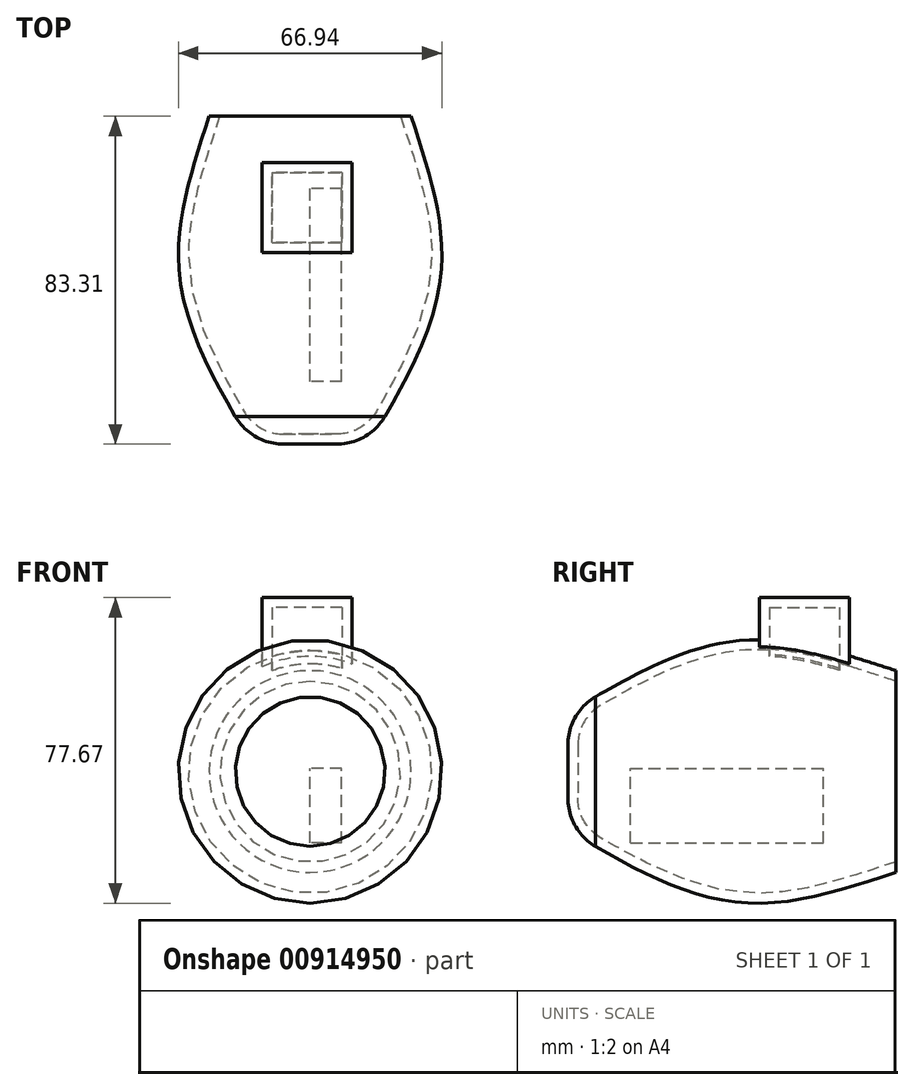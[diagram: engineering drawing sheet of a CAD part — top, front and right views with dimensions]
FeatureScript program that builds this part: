
annotation { "Feature Type Name" : "Feature", "Feature Type Description" : "" }
export const myFeature = defineFeature(function(context is Context, id is Id, definition is map)
    precondition{}
    {
        {
            var Q0;
            Q0=qCreatedBy(makeId("Front.planeOp"),FACE);
            var sketch = newSketch(context, id + "F0", { "sketchPlane" : qUnion([Q0])});
            skCircle(sketch, "E0", {"center": v(0, 0) * mm, "radius": 25.64 * mm});
            skSolve(sketch);
        }
        {
            var Q0;
            Q0=qCreatedBy(makeId("Front.planeOp"),FACE);
            cPlane(context, id + "F1", {"entities" : qUnion([Q0]), "cplaneType" : CPlaneType.OFFSET, "offset" : 38.35 * mm, "width" : 152.4 * mm, "height" : 152.4 * mm});
        }
        {
            var Q0;
            Q0=qCreatedBy(id+"F1.planeOp",FACE);
            cPlane(context, id + "F2", {"entities" : qUnion([Q0]), "cplaneType" : CPlaneType.OFFSET, "offset" : 44.96 * mm, "width" : 152.4 * mm, "height" : 152.4 * mm});
        }
        {
            var Q0;
            Q0=qCreatedBy(id+"F1.planeOp",FACE);
            var sketch = newSketch(context, id + "F3", { "sketchPlane" : qUnion([Q0])});
            skCircle(sketch, "E1", {"center": v(0, 0) * mm, "radius": 33.38 * mm});
            skSolve(sketch);
        }
        {
            var Q0;
            Q0=qCreatedBy(id+"F2.planeOp",FACE);
            var sketch = newSketch(context, id + "F4", { "sketchPlane" : qUnion([Q0])});
            skCircle(sketch, "E2", {"center": v(0, 0) * mm, "radius": 14.84 * mm});
            skSolve(sketch);
        }
        {
            var Q0;
            Q0=makeQuery(id+"F0.imprint","IMPRINT",FACE,{"disambiguationData":[TD([[makeQuery(id+"F0.imprint","IMPRINT",EDGE,{"derivedFrom":sQuery(id+"F0.wireOp",EDGE,"E0")}),1.0]])]});
            var Q1;
            Q1=makeQuery(id+"F3.imprint","IMPRINT",FACE,{"disambiguationData":[TD([[makeQuery(id+"F3.imprint","IMPRINT",EDGE,{"derivedFrom":sQuery(id+"F3.wireOp",EDGE,"E1")}),1.0]])]});
            var Q2;
            Q2=makeQuery(id+"F4.imprint","IMPRINT",FACE,{"disambiguationData":[TD([[makeQuery(id+"F4.imprint","IMPRINT",EDGE,{"derivedFrom":sQuery(id+"F4.wireOp",EDGE,"E2")}),1.0]])]});
            loft(context, id + "F5", {"sheetProfilesArray" : [{ "sheetProfileEntities" : qUnion([Q0]) }, { "sheetProfileEntities" : qUnion([Q1]) }, { "sheetProfileEntities" : qUnion([Q2]) }]});
        }
        {
            var Q0;
            Q0=makeQuery(id+"F5.opLoft","CAP_FACE",FACE,{"disambiguationData":[OSD([makeQuery(id+"F4.imprint","IMPRINT",FACE,{"disambiguationData":[TD([[makeQuery(id+"F4.imprint","IMPRINT",EDGE,{"derivedFrom":sQuery(id+"F4.wireOp",EDGE,"E2")}),1.0]])]})])],"isStart":true});
            fillet(context, id + "F6", {"entities" : qUnion([Q0]), "radius" : 14.2 * mm, "tangentPropagation" : true, "allowEdgeOverflow" : false});
        }
        {
            var Q0;
            Q0=qCreatedBy(makeId("Top.planeOp"),FACE);
            cPlane(context, id + "F7", {"entities" : qUnion([Q0]), "cplaneType" : CPlaneType.OFFSET, "offset" : 18.8 * mm, "width" : 152.4 * mm, "height" : 152.4 * mm});
        }
        {
            var Q0;
            Q0=qCreatedBy(id+"F7.planeOp",FACE);
            var sketch = newSketch(context, id + "F8", { "sketchPlane" : qUnion([Q0])});
            skLineSegment(sketch, "E3.bottom", {"start": v(10.66, -34.64) * mm, "end": v(-12.2, -34.64) * mm});
            skLineSegment(sketch, "E3.top", {"start": v(10.66, -11.78) * mm, "end": v(-12.2, -11.78) * mm});
            skLineSegment(sketch, "E3.left", {"start": v(10.66, -34.64) * mm, "end": v(10.66, -11.78) * mm});
            skLineSegment(sketch, "E3.right", {"start": v(-12.2, -34.64) * mm, "end": v(-12.2, -11.78) * mm});
            skSolve(sketch);
        }
        {
            var Q0;
            Q0 = qSketchRegion(id + "F8", true);
            extrude(context, id + "F9", {"entities" : qUnion([Q0]), "operationType" : NewBodyOperationType.ADD, "depth" : 25.4 * mm, "offsetDistance" : 25.4 * mm});
        }
        {
            var Q0;
            Q0=makeQuery(id+"F5.opLoft","CAP_FACE",FACE,{"disambiguationData":[OSD([makeQuery(id+"F0.imprint","IMPRINT",FACE,{"disambiguationData":[TD([[makeQuery(id+"F0.imprint","IMPRINT",EDGE,{"derivedFrom":sQuery(id+"F0.wireOp",EDGE,"E0")}),1.0]])]})])],"isStart":true});
            shell(context, id + "F10", {"entities" : qUnion([Q0]), "thickness" : 2.54 * mm});
        }
        {
            var Q0;
            Q0=qCreatedBy(makeId("Right.planeOp"),FACE);
            var sketch = newSketch(context, id + "F11", { "sketchPlane" : qUnion([Q0])});
            skLineSegment(sketch, "E4.bottom", {"start": v(-67.41, -18.18) * mm, "end": v(-18.41, -18.18) * mm});
            skLineSegment(sketch, "E4.top", {"start": v(-67.41, 0.82) * mm, "end": v(-18.41, 0.82) * mm});
            skLineSegment(sketch, "E4.left", {"start": v(-67.41, -18.18) * mm, "end": v(-67.41, 0.82) * mm});
            skLineSegment(sketch, "E4.right", {"start": v(-18.41, -18.18) * mm, "end": v(-18.41, 0.82) * mm});
            skSolve(sketch);
        }
        {
            var Q0;
            Q0 = qSketchRegion(id + "F11", true);
            extrude(context, id + "F12", {"entities" : qUnion([Q0]), "depth" : 8 * mm, "offsetDistance" : 25.4 * mm});
        }
    });
